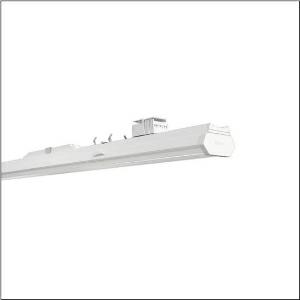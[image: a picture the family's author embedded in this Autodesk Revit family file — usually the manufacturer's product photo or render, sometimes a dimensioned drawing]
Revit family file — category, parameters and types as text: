
# Revit family: licross_r__21_performance_mo_52td16cn49xg_b518
name_source: partatom
category: Lighting Fixtures
units: mm (PartAtom-declared; Revit-internal decimal feet)

## family parameters
Cut with Voids When Loaded = No
Host = Face
Light Source = No
Part Type = Normal
Room Calculation Point = No
Round Connector Dimension = Use Diameter
Shared = No

## types (1)
- --- (1 x LED, 9240 lm, 50.4 W, 4000K)
    Apparent Load = 50 VA
    CIE Flux Codes = 66 88 96 79 100
    Color Rendering = 80
    Color Temperature = 4000K
    Default Elevation = 1800 mm
    Description = Licross® 21 Performance MO, luminaire insert, of sheet steel, galvanised, coil coated, white, length: 1.500mm, width: 120mm, height: 123mm, LED rated luminous flux: 9.240lm, light colour: 840, control gear: ON/OFF Multilumen, CLOi, control gear: ECG Multilumen, with plug, 3-pole, with phase selection, mains connection: 220..240V, AC, 50/60Hz, halogen-free wiring, primary light control with lens, of plastic, primary optical cover: cover, of PMMA, light emission: direct/indirect distribution, primary light characteristic: symmetric, protection rating (complete): IP54, insulation class (complete): insulation class I (protective earthing), certification: CE, ENEC, UKCA, protection symbol: D if used in an environment with non-conductive dust loads with corresponding accessories, impact resistance: IK06, permissible ambient temperature for indoor applications: -35..+45°C, corresponds to IFS (International Featured Standards) requirements for safety and quality in the food industry, reducing of maximum allowable ambient temperature of 5°C with ceiling mounting, LABS conformity tested according to VDMA 24364:2018-05, packaging unit: 1 piece
    Height = 114 mm
    Lamp = 1 x LED
    Lamp Light Flux = 9240 lm
    Lamp Power = 50.4 W
    Lamp count = 1
    Length = 1500 mm
    Luminous efficacy = 183 lm/W
    Manufacturer = Siteco
    ModVariant = No
    Model = 52TD16CN49XG
    Mounting Place = Ceiling
    Mounting Type = Pendant
    Number of Poles = 1
    OnlyDefault = Yes
    Power Factor = 1
    Product Name = Licross® 21 Performance MO
    Product group = luminaire insert
    ProductGroupID = 902
    Protection Class = Protection class I
    Protection Degree = IP 54
    RLX_Detail_Level = 1
    RlxData = <blob elided: 29689 chars, md5=c9e9b519>
    Socket = socket
    Standby Power = 0 W
    System Light Flux = 9240 lm
    System Power = 50 W
    Type Comments = factory setting: luminous flux: 100 % | (A | C | E) | 117 mA
    Type Image = l_1256148.jpg
    URL = http://relux.com
    VarID = @adj_019985
    Voltage = 0 V
    Weight = 0.00 kg
    Width = 120 mm

## geometry (parser evidence)
native form markers: Blend x4, Sweep x12
no freeform markers — native parametric forms only
